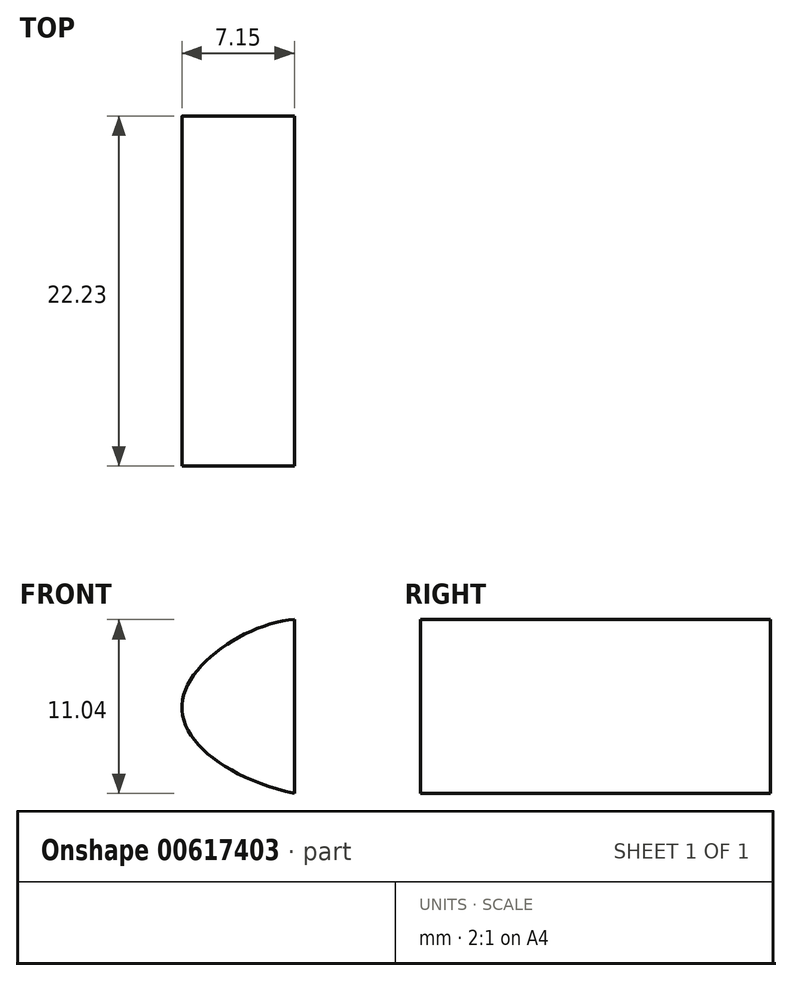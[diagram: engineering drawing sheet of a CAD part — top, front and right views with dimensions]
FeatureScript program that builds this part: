
annotation { "Feature Type Name" : "Feature", "Feature Type Description" : "" }
export const myFeature = defineFeature(function(context is Context, id is Id, definition is map)
    precondition{}
    {
        {
            var Q0;
            Q0=qCreatedBy(makeId("Front.planeOp"),FACE);
            var sketch = newSketch(context, id + "F0", { "sketchPlane" : qUnion([Q0])});
            skLineSegment(sketch, "E0", {"start": v(0, 0) * mm, "end": v(0, 5.94) * mm});
            skLineSegment(sketch, "E1", {"start": v(0, 5.94) * mm, "end": v(0, 11.04) * mm});
            skLineSegment(sketch, "E2", {"start": v(0, 5.94) * mm, "end": v(-7.11, 5.94) * mm});
            skFitSpline(sketch, "E3", {"points": [v(0, 0) * mm, v(-7.11, 5.94) * mm, v(0, 11.04) * mm], "startDerivative": vector(-25.6, 5.55) * mm, "endDerivative": vector(17.38, 1.17) * mm});
            skSolve(sketch);
        }
        {
            var Q0;
            Q0 = qSketchRegion(id + "F0", true);
            extrude(context, id + "F1", {"entities" : qUnion([Q0]), "depth" : 22.22 * mm, "offsetDistance" : 25.4 * mm});
        }
        {
            var Q0;
            Q0=sQuery(id+"F0.wireOp",EDGE,"E3");
            extrude(context, id + "F2", {"bodyType" : ToolBodyType.SURFACE, "surfaceEntities" : qUnion([Q0]), "depth" : 22.22 * mm, "offsetDistance" : 25.4 * mm});
        }
    });
